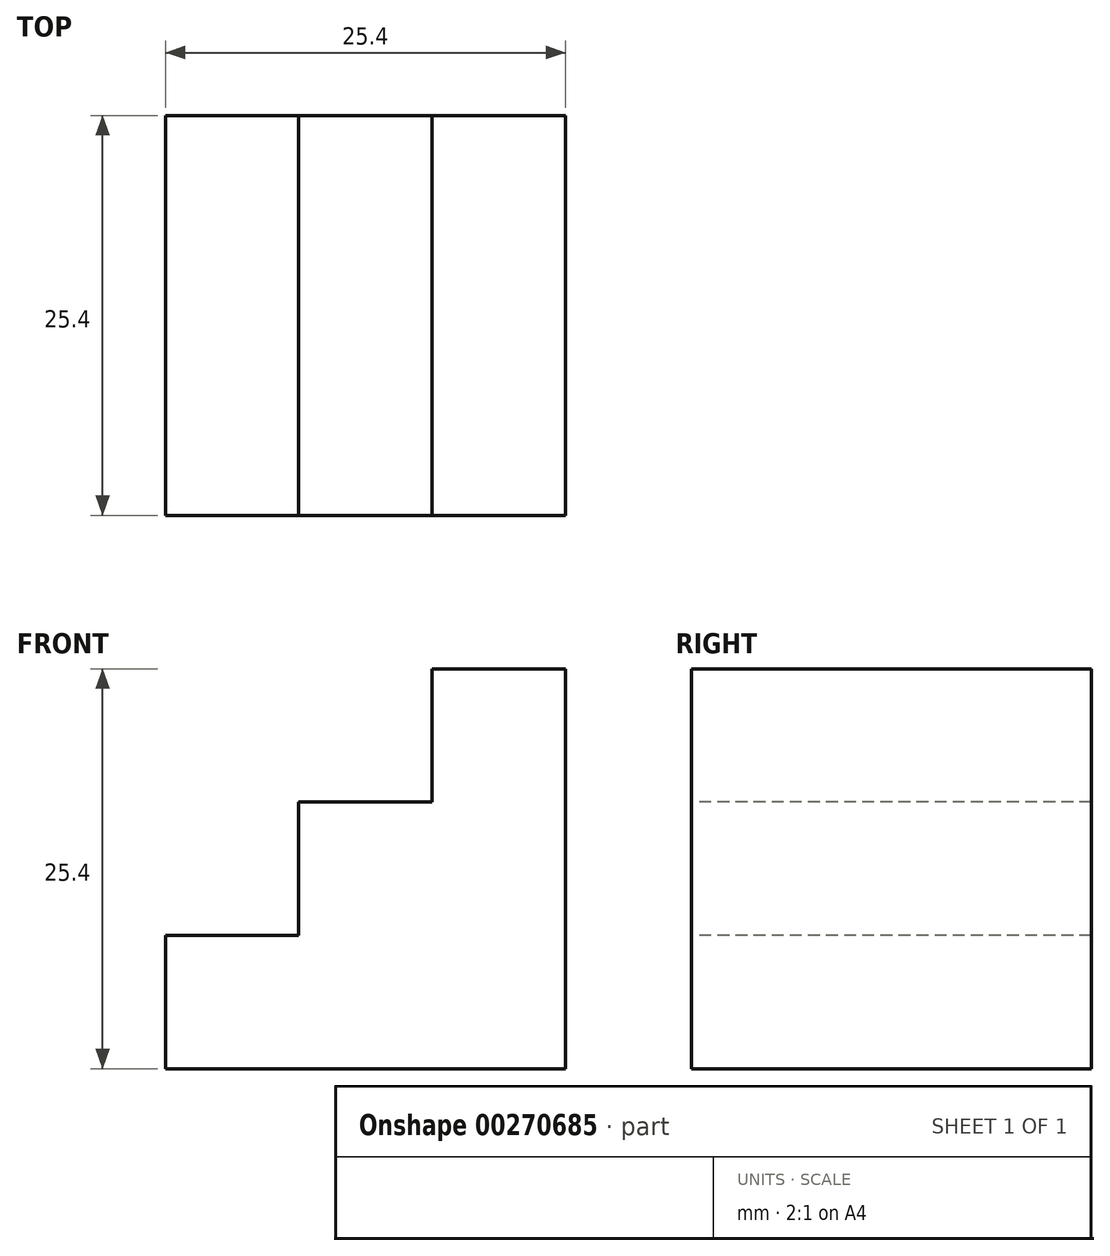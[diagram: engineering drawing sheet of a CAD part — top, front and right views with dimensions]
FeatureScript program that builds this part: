
annotation { "Feature Type Name" : "Feature", "Feature Type Description" : "" }
export const myFeature = defineFeature(function(context is Context, id is Id, definition is map)
    precondition{}
    {
        {
            var Q0;
            Q0=qCreatedBy(makeId("Front.planeOp"),FACE);
            var sketch = newSketch(context, id + "F0", { "sketchPlane" : qUnion([Q0])});
            skLineSegment(sketch, "E0.bottom", {"start": v(0, 0) * mm, "end": v(-25.4, 0) * mm});
            skLineSegment(sketch, "E0.top", {"start": v(0, 25.4) * mm, "end": v(-25.4, 25.4) * mm});
            skLineSegment(sketch, "E0.left", {"start": v(0, 0) * mm, "end": v(0, 25.4) * mm});
            skLineSegment(sketch, "E0.right", {"start": v(-25.4, 0) * mm, "end": v(-25.4, 25.4) * mm});
            skLineSegment(sketch, "E1.bottom", {"start": v(-25.4, 25.4) * mm, "end": v(-8.48, 25.4) * mm});
            skLineSegment(sketch, "E1.top", {"start": v(-25.4, 16.94) * mm, "end": v(-8.48, 16.94) * mm});
            skLineSegment(sketch, "E1.left", {"start": v(-25.4, 25.4) * mm, "end": v(-25.4, 16.94) * mm});
            skLineSegment(sketch, "E1.right", {"start": v(-8.48, 25.4) * mm, "end": v(-8.48, 16.94) * mm});
            skSolve(sketch);
        }
        {
            var Q0;
            Q0=makeQuery(id+"F0.imprint","IMPRINT",FACE,{"disambiguationData":[TD([[makeQuery(id+"F0.imprint","IMPRINT",EDGE,{"derivedFrom":sQuery(id+"F0.wireOp",EDGE,"E0.bottom")}),-1.0]])]});
            extrude(context, id + "F1", {"entities" : qUnion([Q0]), "depth" : 25.4 * mm});
        }
        {
            var Q0;
            Q0=makeQuery(id+"F1.opExtrude","CAP_FACE",FACE,{"disambiguationData":[OSD([sQuery(id+"F0.wireOp",EDGE,"E0.bottom"),sQuery(id+"F0.wireOp",EDGE,"E0.top"),sQuery(id+"F0.wireOp",EDGE,"E0.left"),sQuery(id+"F0.wireOp",EDGE,"E0.right"),sQuery(id+"F0.wireOp",EDGE,"E1.top"),sQuery(id+"F0.wireOp",EDGE,"E1.right")])],"isStart":false});
            var sketch = newSketch(context, id + "F2", { "sketchPlane" : qUnion([Q0])});
            skPoint(sketch, "E2.oppositeSnap0", {"position": v(-16.94, 16.94) * mm});
            skPoint(sketch, "E2.oppositeSnap1", {"position": v(-25.4, 8.47) * mm});
            skLineSegment(sketch, "E2.bottom", {"start": v(-25.4, 16.94) * mm, "end": v(-16.94, 16.94) * mm});
            skLineSegment(sketch, "E2.top", {"start": v(-25.4, 8.47) * mm, "end": v(-16.94, 8.47) * mm});
            skLineSegment(sketch, "E2.left", {"start": v(-25.4, 16.94) * mm, "end": v(-25.4, 8.47) * mm});
            skLineSegment(sketch, "E2.right", {"start": v(-16.94, 16.94) * mm, "end": v(-16.94, 8.47) * mm});
            skSolve(sketch);
        }
        {
            var Q0;
            Q0=makeQuery(id+"F2.imprint","IMPRINT",FACE,{"disambiguationData":[TD([[makeQuery(id+"F2.imprint","IMPRINT",EDGE,{"derivedFrom":sQuery(id+"F2.wireOp",EDGE,"E2.bottom")}),-1.0]])]});
            extrude(context, id + "F3", {"entities" : qUnion([Q0]), "operationType" : NewBodyOperationType.REMOVE, "oppositeDirection" : true, "depth" : 25.4 * mm});
        }
    });
